# Revit family: Lagur Pro
name_source: partatom
category: Plumbing Fixtures
units: mm (PartAtom-declared; Revit-internal decimal feet)

## family parameters
Always vertical = No
Cut with Voids When Loaded = No
OmniClass Number = 23.65.50.11.11.14
OmniClass Title = Water Softeners
Part Type = Normal
Room Calculation Point = No
Round Connector Dimension = Use Diameter
Shared = No
Work Plane-Based = No

## types (8) — shared parameters
HW Connection = No
IP Rating = IP68
Manufacturer = Lagur A/S
URL = https://lagur.dk
Uniclass2015Code = Ss_55_70
Uniclass2015Description = Water distribution and supply system
Vent Connection = No
Version = 1.0
Waste Connection = No
Watt = 40 W
zero-valued in all types: Default Elevation

## per-type parameters (varying)
| type | IfcClassification | Model | Thread | Thread dimension in mm | Weight | X | Y | x |
| DN20 |  | Lagur Pro DN20 | 3/4" RG. | 19 mm | 4.65 kg | 352 mm  [stored 1.15486 ft] | 70 mm  [stored 0.229659 ft] | 32 mm  [stored 0.104987 ft] |
| DN25 |  | Lagur Pro DN25 | 1" RG. | 25 mm  [stored 0.082021 ft] | 4.85 kg | 352 mm  [stored 1.15486 ft] | 70 mm  [stored 0.229659 ft] | 32 mm  [stored 0.104987 ft] |
| DN32 |  | Lagur Pro DN32 | 5/4" RG. | 32 mm  [stored 0.104987 ft] | 7.45 kg | 385 mm  [stored 1.26312 ft] | 89 mm | 41 mm |
| DN40 |  | Lagur Pro DN40 | 1 1/2" RG. | 38 mm | 8.75 kg | 385 mm  [stored 1.26312 ft] | 89 mm | 41 mm |
| DN50 |  | Lagur Pro DN50 | 2" RG. | 51 mm | 9.40 kg | 385 mm  [stored 1.26312 ft] | 114 mm | 54 mm |
| DN65 |  | Lagur Pro DN65 | 2 1/2" RG. | 64 mm | 10.25 kg | 385 mm  [stored 1.26312 ft] | 114 mm | 54 mm |
| DN80 |  | Lagur Pro DN80 | 3" RG. | 76 mm  [stored 0.249344 ft] | 16.50 kg | 400 mm  [stored 1.31234 ft] | 158 mm  [stored 0.518373 ft] | 76 mm  [stored 0.249344 ft] |
| DN100 | IfcFlowTerminal | Lagur Pro DN100 | 4" RG. | 76 mm  [stored 0.249344 ft] | 17.60 kg | 400 mm  [stored 1.31234 ft] | 158 mm  [stored 0.518373 ft] | 76 mm  [stored 0.249344 ft] |

note: [stored X ft] marks values corroborated as IEEE doubles in the binary element streams (Revit-internal decimal feet)

## geometry (parser evidence)
native form markers: Sweep x6
no freeform markers — native parametric forms only
